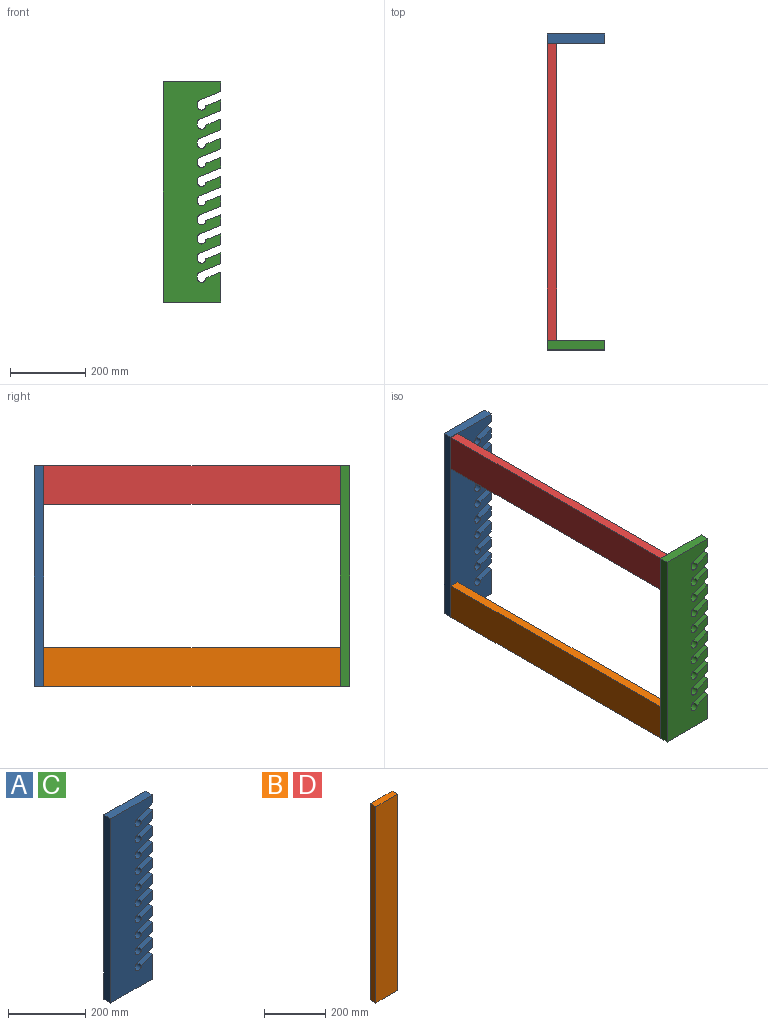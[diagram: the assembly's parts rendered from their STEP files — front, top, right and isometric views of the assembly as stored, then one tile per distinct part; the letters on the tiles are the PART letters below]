
ASSEMBLY  parts=4 mates=9
PART A: 66 faces, bbox 152.4x25.4x584.2 mm
  f0: plane 79.38x25.4mm, normal (1,0,0), area 2016.1mm2, adj f1,f63,f64,f65
  f1: plane 39.69x25.4mm, normal (-0.37,0,0.93), area 1085.7mm2, adj f0,f2,f64,f65
  f2: cylinder r=11.11mm len=25.4mm, axis (0,1,0), area 886.7mm2, adj f1,f3,f64,f65
  f3: plane 25.4x5.81mm, normal (1,0,0), area 147.6mm2, adj f2,f4,f64,f65
  f4: cylinder r=11.11mm len=25.4mm, axis (0,1,0), area 336mm2, adj f3,f5,f64,f65
  f5: plane 54.93x25.4mm, normal (0.37,0,-0.93), area 1502.6mm2, adj f4,f6,f64,f65
  f6: plane 28.58x25.4mm, normal (1,0,0), area 725.8mm2, adj f5,f7,f64,f65
  f7: plane 39.69x25.4mm, normal (-0.37,0,0.93), area 1085.7mm2, adj f6,f8,f64,f65
  f8: cylinder r=11.11mm len=25.4mm, axis (0,1,0), area 886.7mm2, adj f7,f9,f64,f65
  f9: plane 25.4x5.81mm, normal (1,0,0), area 147.6mm2, adj f8,f10,f64,f65
  f10: cylinder r=11.11mm len=25.4mm, axis (0,1,0), area 336mm2, adj f9,f11,f64,f65
  f11: plane 54.93x25.4mm, normal (0.37,0,-0.93), area 1502.6mm2, adj f10,f12,f64,f65
  f12: plane 28.58x25.4mm, normal (1,0,0), area 725.8mm2, adj f11,f13,f64,f65
  f13: plane 39.69x25.4mm, normal (-0.37,0,0.93), area 1085.7mm2, adj f12,f14,f64,f65
  f14: cylinder r=11.11mm len=25.4mm, axis (0,1,0), area 886.7mm2, adj f13,f15,f64,f65
  f15: plane 25.4x5.81mm, normal (1,0,0), area 147.6mm2, adj f14,f16,f64,f65
  f16: cylinder r=11.11mm len=25.4mm, axis (0,1,0), area 336mm2, adj f15,f17,f64,f65
  f17: plane 54.93x25.4mm, normal (0.37,0,-0.93), area 1502.6mm2, adj f16,f18,f64,f65
  f18: plane 28.58x25.4mm, normal (1,0,0), area 725.8mm2, adj f17,f19,f64,f65
  f19: plane 39.69x25.4mm, normal (-0.37,0,0.93), area 1085.7mm2, adj f18,f20,f64,f65
  f20: cylinder r=11.11mm len=25.4mm, axis (0,1,0), area 886.7mm2, adj f19,f21,f64,f65
  f21: plane 25.4x5.81mm, normal (1,0,0), area 147.6mm2, adj f20,f22,f64,f65
  f22: cylinder r=11.11mm len=25.4mm, axis (0,1,0), area 336mm2, adj f21,f23,f64,f65
  f23: plane 54.93x25.4mm, normal (0.37,0,-0.93), area 1502.6mm2, adj f22,f24,f64,f65
  f24: plane 28.58x25.4mm, normal (1,0,0), area 725.8mm2, adj f23,f25,f64,f65
  f25: plane 39.69x25.4mm, normal (-0.37,0,0.93), area 1085.7mm2, adj f24,f26,f64,f65
  f26: cylinder r=11.11mm len=25.4mm, axis (0,1,0), area 886.7mm2, adj f25,f27,f64,f65
  f27: plane 25.4x5.81mm, normal (1,0,0), area 147.6mm2, adj f26,f28,f64,f65
  f28: cylinder r=11.11mm len=25.4mm, axis (0,1,0), area 336mm2, adj f27,f29,f64,f65
  f29: plane 54.93x25.4mm, normal (0.37,0,-0.93), area 1502.6mm2, adj f28,f30,f64,f65
  f30: plane 28.58x25.4mm, normal (1,0,0), area 725.8mm2, adj f29,f31,f64,f65
  f31: plane 39.69x25.4mm, normal (-0.37,0,0.93), area 1085.7mm2, adj f30,f32,f64,f65
  f32: cylinder r=11.11mm len=25.4mm, axis (0,1,0), area 886.7mm2, adj f31,f33,f64,f65
  f33: plane 25.4x5.81mm, normal (1,0,0), area 147.6mm2, adj f32,f34,f64,f65
  f34: cylinder r=11.11mm len=25.4mm, axis (0,1,0), area 336mm2, adj f33,f35,f64,f65
  f35: plane 54.93x25.4mm, normal (0.37,0,-0.93), area 1502.6mm2, adj f34,f36,f64,f65
  f36: plane 28.58x25.4mm, normal (1,0,0), area 725.8mm2, adj f35,f37,f64,f65
  f37: plane 39.69x25.4mm, normal (-0.37,0,0.93), area 1085.7mm2, adj f36,f38,f64,f65
  f38: cylinder r=11.11mm len=25.4mm, axis (0,1,0), area 886.7mm2, adj f37,f39,f64,f65
  f39: plane 25.4x5.81mm, normal (1,0,0), area 147.6mm2, adj f38,f40,f64,f65
  f40: cylinder r=11.11mm len=25.4mm, axis (0,1,0), area 336mm2, adj f39,f41,f64,f65
  f41: plane 54.93x25.4mm, normal (0.37,0,-0.93), area 1502.6mm2, adj f40,f42,f64,f65
  f42: plane 28.58x25.4mm, normal (1,0,0), area 725.8mm2, adj f41,f43,f64,f65
  f43: plane 39.69x25.4mm, normal (-0.37,0,0.93), area 1085.7mm2, adj f42,f44,f64,f65
  f44: cylinder r=11.11mm len=25.4mm, axis (0,1,0), area 886.7mm2, adj f43,f45,f64,f65
  f45: plane 25.4x5.81mm, normal (1,0,0), area 147.6mm2, adj f44,f46,f64,f65
  f46: cylinder r=11.11mm len=25.4mm, axis (0,1,0), area 336mm2, adj f45,f47,f64,f65
  f47: plane 54.93x25.4mm, normal (0.37,0,-0.93), area 1502.6mm2, adj f46,f48,f64,f65
  f48: plane 28.58x25.4mm, normal (1,0,0), area 725.8mm2, adj f47,f49,f64,f65
  f49: plane 39.69x25.4mm, normal (-0.37,0,0.93), area 1085.7mm2, adj f48,f50,f64,f65
  f50: cylinder r=11.11mm len=25.4mm, axis (0,1,0), area 886.7mm2, adj f49,f51,f64,f65
  f51: plane 25.4x5.81mm, normal (1,0,0), area 147.6mm2, adj f50,f52,f64,f65
  f52: cylinder r=11.11mm len=25.4mm, axis (0,1,0), area 336mm2, adj f51,f53,f64,f65
  f53: plane 54.93x25.4mm, normal (0.37,0,-0.93), area 1502.6mm2, adj f52,f54,f64,f65
  f54: plane 28.58x25.4mm, normal (1,0,0), area 725.8mm2, adj f53,f55,f64,f65
  f55: plane 39.69x25.4mm, normal (-0.37,0,0.93), area 1085.7mm2, adj f54,f56,f64,f65
  f56: cylinder r=11.11mm len=25.4mm, axis (0,1,0), area 886.7mm2, adj f55,f57,f64,f65
  f57: plane 25.4x5.81mm, normal (1,0,0), area 147.6mm2, adj f56,f58,f64,f65
  f58: cylinder r=11.11mm len=25.4mm, axis (0,1,0), area 336mm2, adj f57,f59,f64,f65
  f59: plane 54.93x25.4mm, normal (0.37,0,-0.93), area 1502.6mm2, adj f58,f60,f64,f65
  f60: plane 25.4x25.4mm, normal (1,0,0), area 645.2mm2, adj f59,f61,f64,f65
  f61: plane 152.4x25.4mm, normal (0,0,1), area 3871mm2, adj f60,f62,f64,f65
  f62: plane 584.2x25.4mm, normal (-1,0,0), area 14838.7mm2, adj f61,f63,f64,f65
  f63: plane 152.4x25.4mm, normal (0,0,-1), area 3871mm2, adj f0,f62,f64,f65
  f64: plane 584.2x152.4mm, normal (0,-1,0), area 74421.3mm2, adj f0,f1,f2,f3,f4,f5,f6,f7
  f65: plane 584.2x152.4mm, normal (0,1,0), area 74421.3mm2, adj f0,f1,f2,f3,f4,f5,f6,f7
PART B: 6 faces, bbox 101.6x25.4x787.4 mm
  f0: plane 787.4x25.4mm, normal (1,0,0), area 20000mm2, adj f1,f3,f4,f5
  f1: plane 101.6x25.4mm, normal (0,0,1), area 2580.6mm2, adj f0,f2,f4,f5
  f2: plane 787.4x25.4mm, normal (-1,0,0), area 20000mm2, adj f1,f3,f4,f5
  f3: plane 101.6x25.4mm, normal (0,0,-1), area 2580.6mm2, adj f0,f2,f4,f5
  f4: plane 787.4x101.6mm, normal (0,-1,0), area 79999.8mm2, adj f0,f1,f2,f3
  f5: plane 787.4x101.6mm, normal (0,1,0), area 79999.8mm2, adj f0,f1,f2,f3
PART C: same geometry as A
PART D: same geometry as B
PLACE A t=(-304.9,-1544.61,-446.99)mm
PLACE B rot(axis=(0.58,-0.58,0.58),120deg) t=(-381.1,-1963.71,-688.29)mm
PLACE C t=(-304.9,-2357.41,-446.99)mm
PLACE D rot(axis=(0.58,-0.58,0.58),120deg) t=(-381.1,-1963.71,-205.69)mm
MATE planar B.f2 <-> C.f63  axis (0,0,-1) through (-368.4,-1963.71,-739.09)mm
MATE planar A.f61 <-> C.f61  axis (0,0,1) through (-304.9,-1557.31,-154.89)mm
MATE planar D.f0 <-> C.f61  axis (0,0,1) through (-368.4,-1963.71,-154.89)mm
MATE planar A.f62 <-> C.f62  axis (-1,0,0) through (-381.1,-1557.31,-446.99)mm
MATE planar C.f65 <-> D.f1  axis (0,1,0) through (-304.9,-2357.41,-154.89)mm
MATE planar B.f1 <-> C.f65  axis (0,-1,0) through (-368.4,-2357.41,-688.29)mm
MATE planar D.f3 <-> A.f64  axis (0,1,0) through (-381.1,-1570.01,-154.89)mm
MATE planar D.f5 <-> C.f62  axis (-1,0,0) through (-381.1,-2357.41,-205.69)mm
MATE planar B.f5 <-> C.f62  axis (-1,0,0) through (-381.1,-1963.71,-688.29)mm
